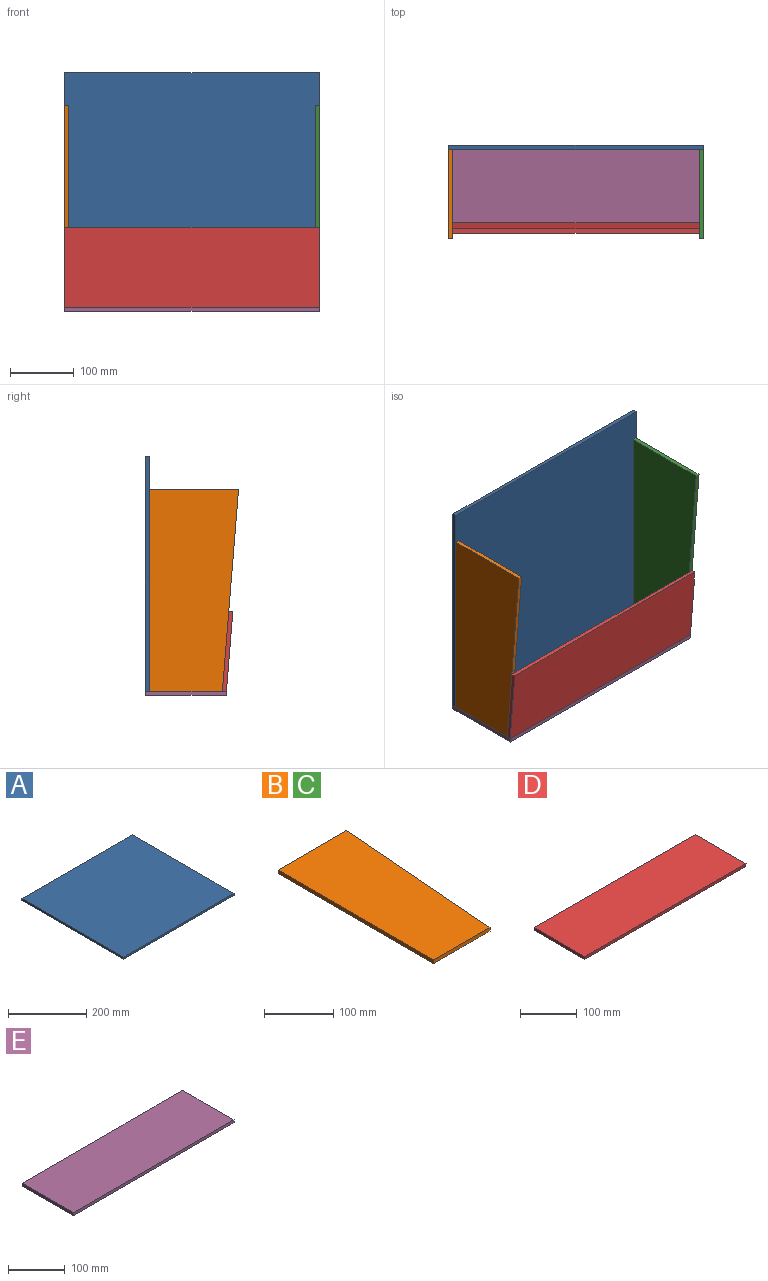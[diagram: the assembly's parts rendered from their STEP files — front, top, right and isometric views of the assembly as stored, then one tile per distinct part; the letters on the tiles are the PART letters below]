
ASSEMBLY  parts=5 mates=4
PART A: 6 faces, bbox 400.1x368.3x6.4 mm
  f0: plane 368.3x6.35mm, normal (-1,0,0), area 2338.7mm2, adj f1,f3,f4,f5
  f1: plane 400.05x6.35mm, normal (0,-1,0), area 2540.3mm2, adj f0,f2,f4,f5
  f2: plane 368.3x6.35mm, normal (1,0,0), area 2338.7mm2, adj f1,f3,f4,f5
  f3: plane 400.05x6.35mm, normal (0,1,0), area 2540.3mm2, adj f0,f2,f4,f5
  f4: plane 400.05x368.3mm, normal (0,0,1), area 147338.4mm2, adj f0,f1,f2,f3
  f5: plane 400.05x368.3mm, normal (0,0,-1), area 147338.4mm2, adj f0,f1,f2,f3
PART B: 6 faces, bbox 139.7x317.5x6.4 mm
  f0: plane 139.7x6.35mm, normal (0,1,0), area 887.1mm2, adj f1,f3,f4,f5
  f1: plane 317.5x6.35mm, normal (-1,0,0), area 2016.1mm2, adj f0,f2,f4,f5
  f2: plane 114.3x6.35mm, normal (0,-1,0), area 725.8mm2, adj f1,f3,f4,f5
  f3: plane 317.5x25.4mm, normal (1,-0.08,0), area 2022.6mm2, adj f0,f2,f4,f5
  f4: plane 317.5x139.7mm, normal (0,0,1), area 40322.5mm2, adj f0,f1,f2,f3
  f5: plane 317.5x139.7mm, normal (0,0,-1), area 40322.5mm2, adj f0,f1,f2,f3
PART C: same geometry as B
PART D: 6 faces, bbox 400.1x126.5x6.4 mm
  f0: plane 126.49x6.35mm, normal (-1,0,0), area 800mm2, adj f1,f3,f4,f5
  f1: plane 400.05x125.98mm, normal (0,0,1), area 50399.9mm2, adj f0,f2,f4,f5
  f2: plane 126.49x6.35mm, normal (1,0,0), area 800mm2, adj f1,f3,f4,f5
  f3: plane 400.05x125.98mm, normal (0,0,-1), area 50399.9mm2, adj f0,f2,f4,f5
  f4: plane 400.05x6.35mm, normal (0,1,0.08), area 2548.4mm2, adj f0,f1,f2,f3
  f5: plane 400.05x6.35mm, normal (0,-1,-0.08), area 2548.4mm2, adj f0,f1,f2,f3
PART E: 6 faces, bbox 400.1x127x6.4 mm
  f0: plane 127x6.35mm, normal (-1,0,0), area 806.5mm2, adj f1,f3,f4,f5
  f1: plane 400.05x6.35mm, normal (0,-1,0), area 2540.3mm2, adj f0,f2,f4,f5
  f2: plane 127x6.35mm, normal (1,0,0), area 806.5mm2, adj f1,f3,f4,f5
  f3: plane 400.05x6.35mm, normal (0,1,0), area 2540.3mm2, adj f0,f2,f4,f5
  f4: plane 400.05x127mm, normal (0,0,1), area 50806.3mm2, adj f0,f1,f2,f3
  f5: plane 400.05x127mm, normal (0,0,-1), area 50806.3mm2, adj f0,f1,f2,f3
PLACE A rot(axis=(1,0,0),90deg) t=(0.26,62.06,184.94)mm
PLACE B rot(axis=(0.58,-0.58,-0.58),120deg) t=(-193.42,55.71,138.11)mm
PLACE C rot(axis=(0.58,-0.58,-0.58),120deg) t=(200.28,55.71,138.11)mm
PLACE D rot(axis=(0,-0.68,-0.73),180deg) t=(0.26,-69.95,63.07)mm
PLACE E t=(0.26,-1.44,-5.56)mm fixed
MATE fastened A.f1 <-> E.f4  axis (0,0,-1) through (0.26,62.06,0.79)mm
MATE fastened D.f1 <-> C.f3  axis (0,1,0.08) through (200.28,-58.59,0.79)mm
MATE fastened C.f1 <-> A.f4  axis (0,1,0) through (200.28,55.71,0.79)mm
MATE fastened B.f1 <-> A.f4  axis (0,1,0) through (-199.77,55.71,0.79)mm
